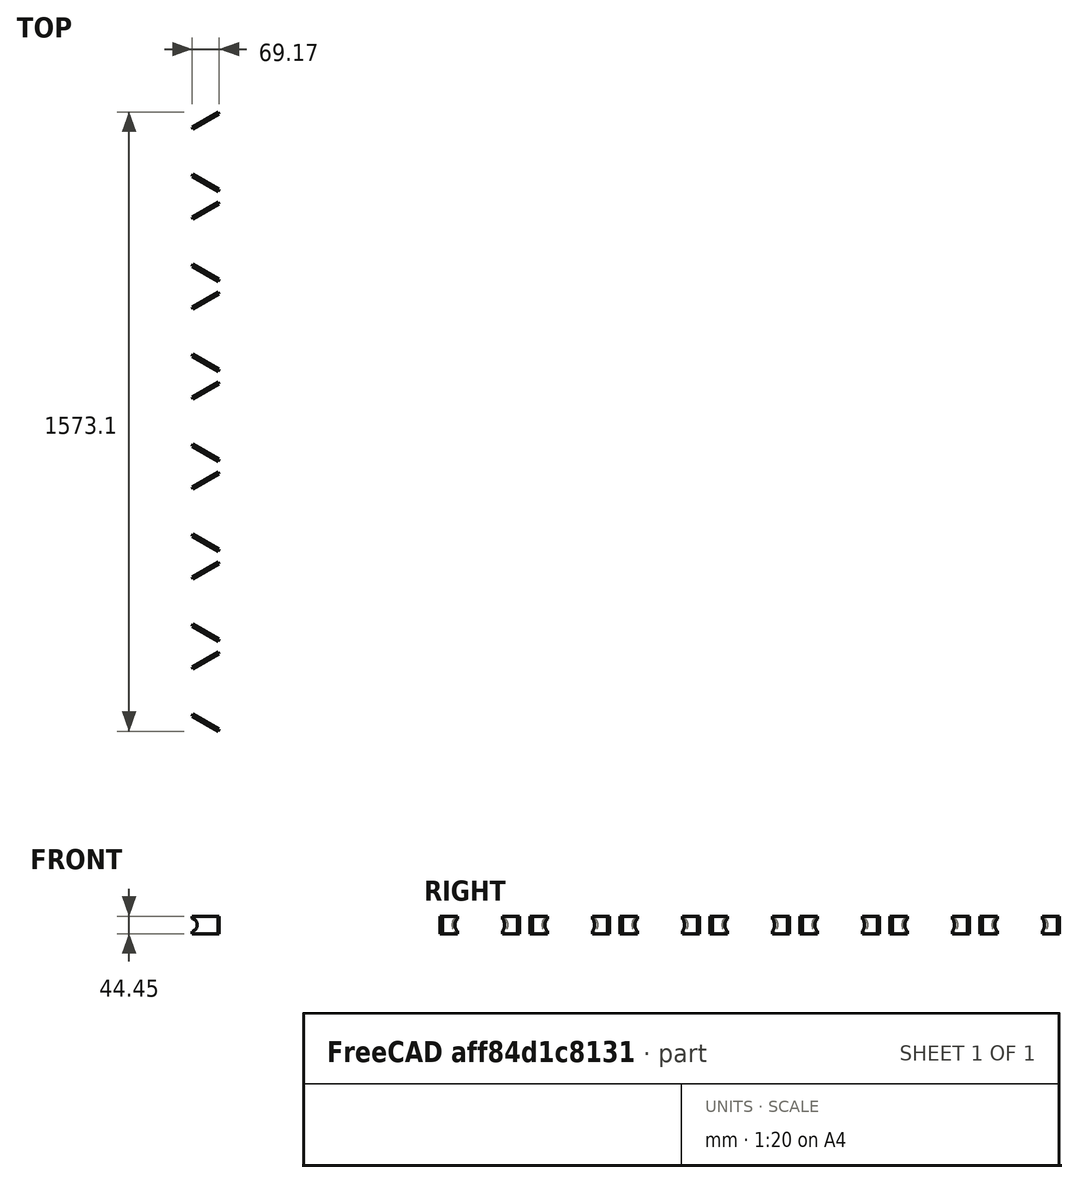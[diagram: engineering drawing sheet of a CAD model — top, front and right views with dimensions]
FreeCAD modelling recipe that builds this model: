
FCSTD DOCUMENT  (FreeCAD 0.17R13522 (Git))
Label: gussets
License: CreativeCommons Attribution
LicenseURL: http://creativecommons.org/licenses/by/4.0/
objects: Part::FeaturePython×4, Part::Box×1, Part::Cut×1, Part::Mirroring×1, Part::MultiFuse×1
note: 8 computed .brp shape members not serialized (recipe doc carries the construction recipe); baked Part::Feature solids carry a one-line shape summary decoded from their .brp

FEATURE [Part::FeaturePython] Tube_1_625_sch80_01  label="Tube_1_315_0.133thick"  # a2plus imported part (geometry in sourceFile) (typed FeaturePython)
  Placement = pos=(780.915,0,22.4829) rot=(-0.624695,0,0.780869;3.14159rad)
  fixedPosition = false
  sourceFile = <userpath>/Freecad_Git/Grapples/01_Hardware/Mechanical_Parts/Tube 1.315 0.133 thick for tines.fcstd
  timeLastImport = 1.52609e+09
  updateColors = true
FEATURE [Part::FeaturePython] gussets_01  label="Inside gussets"  # a2plus imported part (geometry in sourceFile) (typed FeaturePython)
  Placement = pos=(780.915,228.6,-21.9671) rot=(0,0,1;0rad)
  fixedPosition = false
  sourceFile = <userpath>/Freecad_Git/Grapples/01_Hardware/Mechanical_Parts/Inside Gussets.fcstd
  timeLastImport = 1.52577e+09
  updateColors = true
FEATURE [Part::Box] Box  label="Cube"
  AttacherType = Attacher::AttachEngine3D
  Height = 44.45
  Length = 76.2
  Placement = pos=(787.4,177.8,0) rot=(0,0,1;0.523599rad)
  Width = 6.35
FEATURE [Part::FeaturePython] Cutout  label="Used for dxf export small gusset"  # WARN: FeaturePython — macro-defined, semantics opaque (R4)
  Base = -> Box
  Tolerance = 0
  Tool = -> Tube_1_625_sch80_01
FEATURE [Part::Cut] Cut
  Base = -> Cutout
  Placement = pos=(0,-120.65,0) rot=(0,0,1;0rad)
  Tool = -> gussets_01
FEATURE [Part::Mirroring] Part__Mirroring  label="Cut (Mirror #1)"
  Base = (0,0,0)
  Normal = (0,1,0)
  Source = -> Cut
FEATURE [Part::MultiFuse] Fusion
  Shapes = -> [Cut,Part__Mirroring]
FEATURE [Part::FeaturePython] Array  # Draft array (typed FeaturePython)
  Angle = 360
  ArrayType = 0
  Axis = (0,0,1)
  Base = -> Fusion
  Center = (0,0,0)
  Fuse = false
  IntervalAxis = (0,0,0)
  IntervalX = (1,0,0)
  IntervalY = (0,228.6,0)
  IntervalZ = (0,0,0)
  NumberPolar = 1
  NumberX = 1
  NumberY = 7
  NumberZ = 1
